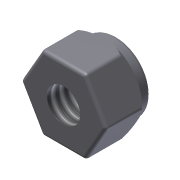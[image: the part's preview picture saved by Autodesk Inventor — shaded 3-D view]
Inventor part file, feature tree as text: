
AUTODESK INVENTOR PART (.ipt)
format: ipt  version: 2011 (Build 150239000, 239)  size: 179,712 bytes
history: native  units: in
note: dims shown in document units (in); Inventor stores cm internally (conversion verified against a paired STEP export)
features: sketch x5, extrude x3, fillet x2, hole x1, revolve x1, projected_geometry x1
ambient origin geometry x8: Origin, YZ Plane, XZ Plane, XY Plane, X Axis, Y Axis, Z Axis, Center Point
bodies: Solid1 (feature_tree)
feature tree (13):
  extrude  "Extrusion1"  Depth=0.25in TaperAngle=0.0deg
  extrude  "Extrusion2"  Depth=0.18in
  sketch  "Sketch8"  dims[d17=0.196in d18=0.172in d19=0.375in d20=0.25in d21=0.5635in d22=1.0in d23=0.8108in d24=0.18in]
  hole  "Hole2"  [1 undecoded]
  revolve  "Revolution2"  [1 undecoded]
  fillet  "Fillet1"  Radius=0.25in
  fillet  "Fillet2"  Radius=0.01in
  extrude  "Extrusion4"  [1 undecoded]
  sketch  "Sketch1"  dims[d0=0.4375in d1=0.25in d2=0.0in]
  sketch  "Sketch3"  dims[d4=0.0625in d5=0.0in]
  sketch  "Sketch9"  dims[d25=90.0deg d26=0.02in]
  sketch  "Sketch10"  dims[d27=0.02in d28=0.4in d29=0.25in d30=0.01in d31=0.0in]
  projected_geometry  "Projected Loop8"
note: 3 required parameter values undecoded (feature->parameter linkage not recoverable at this tier; creation-order binding heuristic only, values carry confidence <= 0.55)